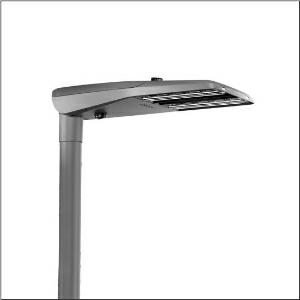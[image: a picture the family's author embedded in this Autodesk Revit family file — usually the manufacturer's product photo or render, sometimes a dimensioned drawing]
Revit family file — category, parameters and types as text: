
# Revit family: streetlight_sl_11_iq_midi___st1_2a_5xc3a51y08me_2b41
name_source: partatom
category: Lighting Fixtures
units: mm (PartAtom-declared; Revit-internal decimal feet)

## family parameters
Cut with Voids When Loaded = No
Host = Face
Light Source = No
Part Type = Normal
Room Calculation Point = No
Round Connector Dimension = Use Diameter
Shared = No

## types (1)
- --- (1 x LED, 18110 lm, 122.7 W, 3000K)
    Apparent Load = 123 VA
    CIE Flux Codes = 32 70 96 100 100
    Color Rendering = 70
    Color Temperature = 3000K
    Default Elevation = 1800 mm
    Description = Streetlight SL 11 iQ midi, mast luminaire, primary light control with 3 zone facetted reflector, of plastic, silver coated, highly specular, primary optical cover: cover, of PMMA, transparent, light distribution: ST1.2a, light emission: direct distribution, primary light characteristic: asymmetric, installation type: post-top, side-entry, lamps: LED, High Power LED, rated values: 18.110lm | 122,7W | 147,6lm/W (begin service life); end service life: 18.110lm | 130,2W; at 50% lumin. flux: 9.055lm | 56,1W | 161,4lm/W, colour temperature: 3000K, colour rendering: CRI > 70, light colour: 730, light setting 1 begin service life: 100% | 18.110lm | 122,7W | 147,6lm/W | 3.000K, light setting 1 end service life: 130,2W, further light settings possible, control: pre-setting: logarithmic dimming characteristic, Street-Remote, Auto-Match, Temp-Guard, Lumen-Switch, Night-Set, Smart-Wire, Light-Fading, Desk-Remote (wireless, voltage-free reading and setting of iQ features in the workshop via application-optimized NFC function/RFID function), optimised constant luminous flux control (CLO 2.0), with cable H07RN-F 5x 1.5mm², mains connection: 230..240V, AC, 50/60Hz, connection cable pre-assembled, cable length: 12,5m, luminaire housing, of diecast aluminium, powder-coated, Siteco® metallic grey (DB 702S), please order mast flange separately, inclination adjustable without tools: 0°, 5°, 10°, 15° (post-top) | 0°, -5°, -10°, -15° (side-entry), sealing non-destructively replaceable, multi-level sealing system, length: 780mm, width: 376mm, height: 118mm, mast flange for spigot size: 42mm (side-entry): 5XC10008XM4, 60/48mm (side-entry/post-top): 5XC10108XM2, 76/60mm (side-entry/post-top): 5XC10108XM1, equipment: Power, Smart Interface below and above, protection rating (complete): IP66, insulation class (complete): insulation class II (safety insulation), certification: CE, ENEC, ENEC+, VDE, UKCA, impact resistance: IK10, permissible operating ambient temperature for outdoor applications: -25..+50°C, standard-compliant lighting for roads and squares, Environmental Product Declaration (EPD) tested and certified by an independent institute, packaging unit: 1 piece

Light Distribution: ST1.2a
    Height = 118 mm
    Lamp = 1 x LED
    Lamp Light Flux = 18110 lm
    Lamp Power = 122.7 W
    Lamp count = 1
    Length = 780 mm
    Luminous efficacy = 148 lm/W
    Manufacturer = Siteco
    ModVariant = No
    Model = 5XC3A51Y08ME
    Number of Poles = 1
    OnlyDefault = Yes
    Power Factor = 1
    Product Name = Streetlight SL 11 iQ midi | ST1.2a
    Product group = mast luminaire | pylon top
    ProductGroupID = 6100
    Protection Class = Protection class II
    Protection Degree = IP 66
    RLX_Detail_Level = 1
    RLX_Emergency_Light_Flux = 0 lm
    RLX_Emergency_Type = 0
    RLX_Emergency_Type_DB = No
    RlxData = <blob elided: 69997 chars, md5=7435e13e>
    Socket = socket
    Standby Power = 0 W
    System Light Flux = 18111 lm
    System Power = 123 W
    Type Comments = factory setting: luminous flux: 100 % | dim-lin: 254 | 553 mA
    Type Image = l_1004429.jpg
    URL = http://relux.com
    VarID = @adj_133266
    Voltage = 0 V
    Weight = 0.00 kg
    Width = 376 mm

## geometry (parser evidence)
native form markers: Blend x4, Sweep x10
no freeform markers — native parametric forms only
